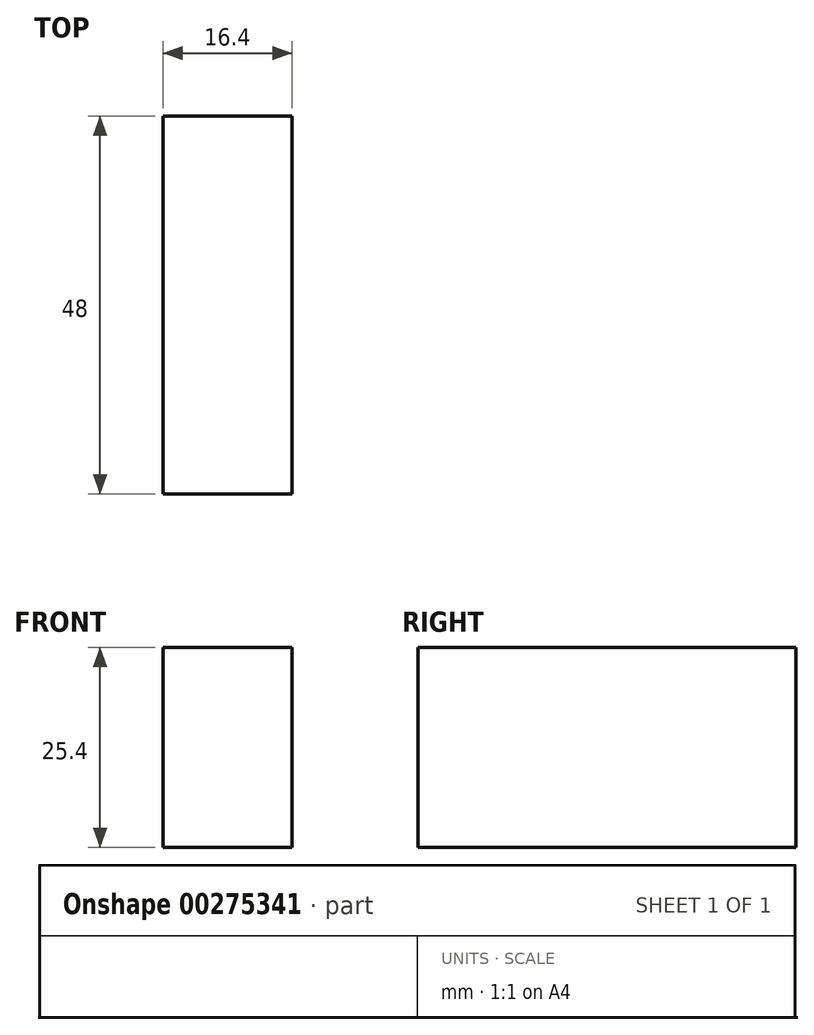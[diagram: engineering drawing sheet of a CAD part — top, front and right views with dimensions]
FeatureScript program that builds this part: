
annotation { "Feature Type Name" : "Feature", "Feature Type Description" : "" }
export const myFeature = defineFeature(function(context is Context, id is Id, definition is map)
    precondition{}
    {
        {
            var Q0;
            Q0=qCreatedBy(makeId("Top.planeOp"),FACE);
            var sketch = newSketch(context, id + "F0", { "sketchPlane" : qUnion([Q0])});
            skLineSegment(sketch, "E0.bottom", {"start": v(0, 0) * mm, "end": v(-16.4, 0) * mm});
            skLineSegment(sketch, "E0.top", {"start": v(0, 48) * mm, "end": v(-16.4, 48) * mm});
            skLineSegment(sketch, "E0.left", {"start": v(0, 0) * mm, "end": v(0, 48) * mm});
            skLineSegment(sketch, "E0.right", {"start": v(-16.4, 0) * mm, "end": v(-16.4, 48) * mm});
            skSolve(sketch);
        }
        {
            var Q0;
            Q0=makeQuery(id+"F0.imprint","IMPRINT",FACE,{"disambiguationData":[TD([[makeQuery(id+"F0.imprint","IMPRINT",EDGE,{"derivedFrom":sQuery(id+"F0.wireOp",EDGE,"E0.bottom")}),-1.0]])]});
            extrude(context, id + "F1", {"entities" : qUnion([Q0]), "depth" : 25.4 * mm});
        }
    });
